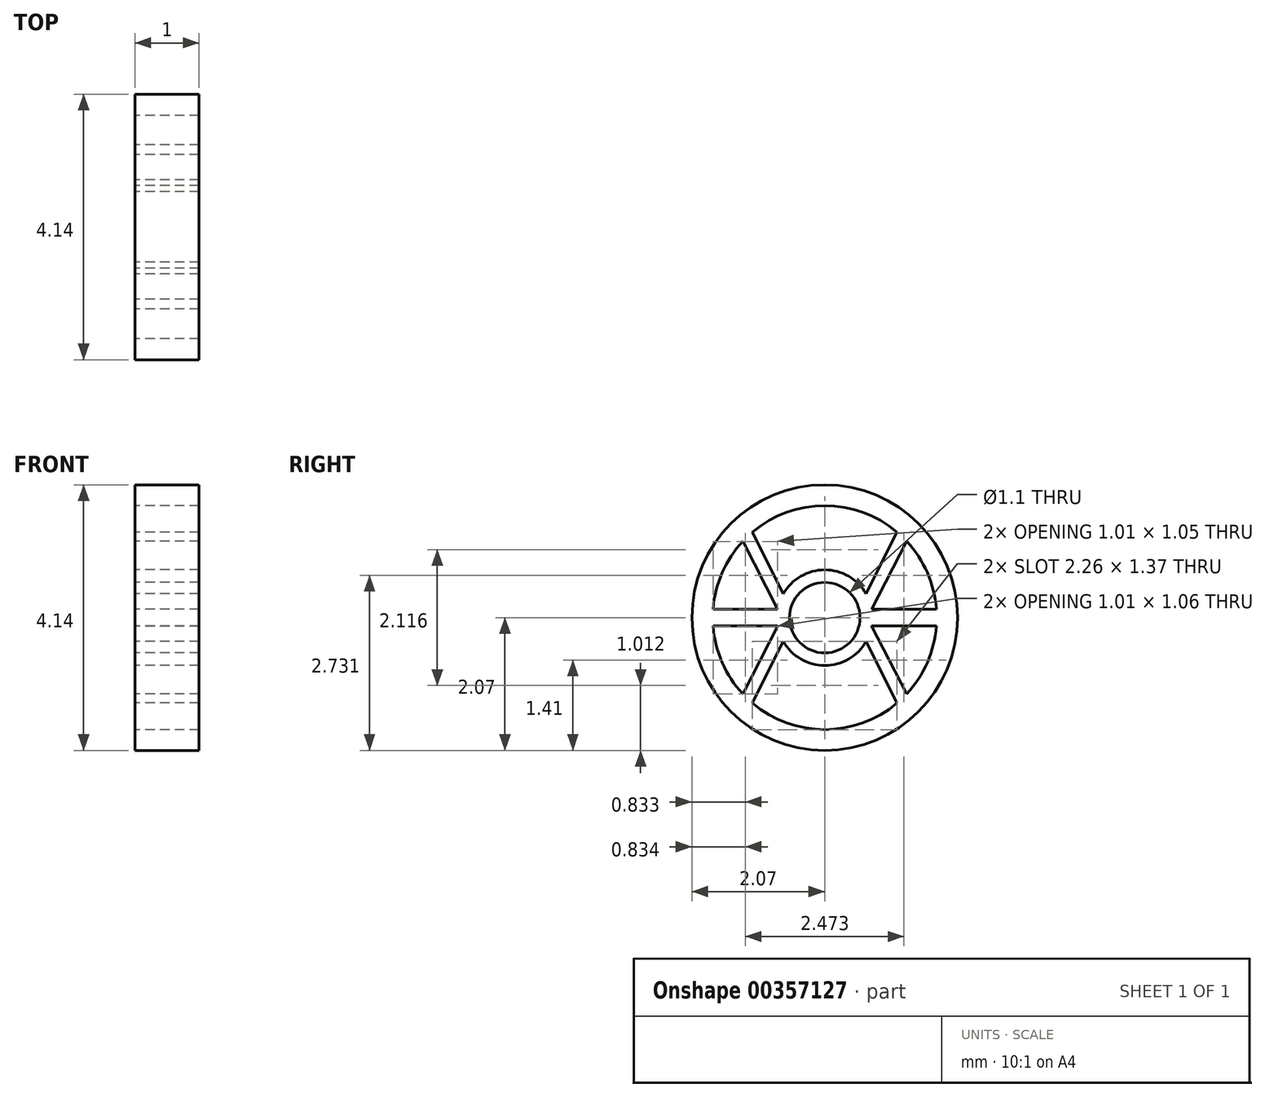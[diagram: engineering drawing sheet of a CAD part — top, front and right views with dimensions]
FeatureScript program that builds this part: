
annotation { "Feature Type Name" : "Feature", "Feature Type Description" : "" }
export const myFeature = defineFeature(function(context is Context, id is Id, definition is map)
    precondition{}
    {
        {
            var Q0;
            Q0=qCreatedBy(makeId("Right.planeOp"),FACE);
            var sketch = newSketch(context, id + "F0", { "sketchPlane" : qUnion([Q0])});
            skCircle(sketch, "E0", {"center": v(0, 0) * mm, "radius": 2.07 * mm});
            skArc(sketch, "E1", {"start": v(-1.28, 1.19) * mm, "mid": v(-1.6, 0.7) * mm, "end": v(-1.74, 0.13) * mm});
            skArc(sketch, "E2", {"start": v(0.65, 0.37) * mm, "mid": v(0, 0.74) * mm, "end": v(-0.65, 0.37) * mm});
            skLineSegment(sketch, "E3", {"start": v(-0.73, 0.13) * mm, "end": v(-1.74, 0.13) * mm});
            skLineSegment(sketch, "E4", {"start": v(-0.73, -0.13) * mm, "end": v(-1.74, -0.13) * mm});
            skLineSegment(sketch, "E5.MirrorCS", {"start": v(0.73, 0.13) * mm, "end": v(1.74, 0.13) * mm});
            skLineSegment(sketch, "E6.MirrorCS", {"start": v(0.73, -0.13) * mm, "end": v(1.74, -0.13) * mm});
            skLineSegment(sketch, "E7", {"start": v(-0.73, 0.13) * mm, "end": v(-1.28, 1.19) * mm});
            skLineSegment(sketch, "E8", {"start": v(-0.65, 0.37) * mm, "end": v(-1.13, 1.33) * mm});
            skLineSegment(sketch, "E9.MirrorCS", {"start": v(0.73, 0.13) * mm, "end": v(1.28, 1.19) * mm});
            skLineSegment(sketch, "E10.MirrorCS", {"start": v(0.65, 0.37) * mm, "end": v(1.13, 1.33) * mm});
            skLineSegment(sketch, "E11.MirrorCS", {"start": v(-0.73, -0.13) * mm, "end": v(-1.28, -1.19) * mm});
            skLineSegment(sketch, "E12.MirrorCS", {"start": v(-0.65, -0.37) * mm, "end": v(-1.13, -1.33) * mm});
            skLineSegment(sketch, "E13.MirrorCS", {"start": v(0.65, -0.37) * mm, "end": v(1.13, -1.33) * mm});
            skLineSegment(sketch, "E14.MirrorCS", {"start": v(0.73, -0.13) * mm, "end": v(1.28, -1.19) * mm});
            skArc(sketch, "E15.trimOffspring", {"start": v(-1.74, -0.13) * mm, "mid": v(-1.6, -0.7) * mm, "end": v(-1.28, -1.19) * mm});
            skArc(sketch, "E16.trimOffspring", {"start": v(-1.13, -1.33) * mm, "mid": v(0, -1.75) * mm, "end": v(1.13, -1.33) * mm});
            skArc(sketch, "E17.trimOffspring", {"start": v(1.13, 1.33) * mm, "mid": v(0, 1.75) * mm, "end": v(-1.13, 1.33) * mm});
            skArc(sketch, "E18.trimOffspring", {"start": v(1.74, 0.13) * mm, "mid": v(1.6, 0.7) * mm, "end": v(1.28, 1.19) * mm});
            skArc(sketch, "E19.trimOffspring", {"start": v(1.28, -1.19) * mm, "mid": v(1.6, -0.7) * mm, "end": v(1.74, -0.13) * mm});
            skCircle(sketch, "E20", {"center": v(0, 0) * mm, "radius": 0.55 * mm});
            skArc(sketch, "E21.trimOffspring", {"start": v(-0.65, -0.37) * mm, "mid": v(0, -0.74) * mm, "end": v(0.65, -0.37) * mm});
            skArc(sketch, "E22.trimOffspring", {"start": v(0.73, -0.13) * mm, "mid": v(0.73, -0.13) * mm, "end": v(0.73, -0.13) * mm});
            skArc(sketch, "E23.trimOffspring", {"start": v(-0.73, -0.13) * mm, "mid": v(-0.73, -0.13) * mm, "end": v(-0.73, -0.13) * mm});
            skSolve(sketch);
        }
        {
            var Q0;
            Q0 = qSketchRegion(id + "F0", true);
            extrude(context, id + "F1", {"entities" : qUnion([Q0]), "depth" : 1 * mm});
        }
    });
